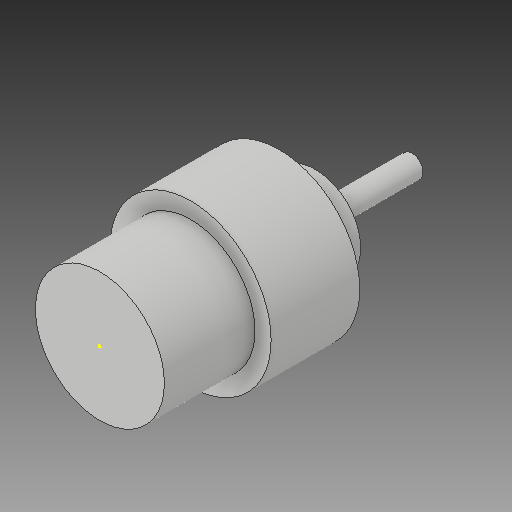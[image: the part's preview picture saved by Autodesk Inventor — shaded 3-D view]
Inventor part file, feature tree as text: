
AUTODESK INVENTOR PART (.ipt)
format: ipt  version: 2019 (Build 230136000, 136)  size: 128,000 bytes
history: native  units: in
note: dims shown in document units (in); Inventor stores cm internally (conversion verified against a paired STEP export)
features: sketch x6, extrude x4
ambient origin geometry x8: Origin, YZ Plane, XZ Plane, XY Plane, X Axis, Y Axis, Z Axis, Center Point
bodies: Solid1 (feature_tree)
feature tree (10):
  sketch  "Sketch1"  dims[d0=1.5748in d1=0.8661in d2=0.0in]
  extrude  "Extrusion1"  Depth=0.8661in TaperAngle=0.0deg
  extrude  "Extrusion2"  Depth=0.8858in TaperAngle=0.0deg
  sketch  "Sketch4"  dims[d11=0.2165in d12=0.9449in d13=0.0in]
  extrude  "Extrusion3"  Depth=0.3543in TaperAngle=0.0deg
  extrude  "Extrusion4"  Depth=0.9449in TaperAngle=0.0deg
  sketch  "Sketch2"  dims[d3=1.2598in d4=0.8858in d5=0.0in]
  sketch  "Sketch3"  dims[d8=0.8858in d9=0.3543in d10=0.0in]
  sketch  "Sketch5"
  sketch  "Sketch6"
